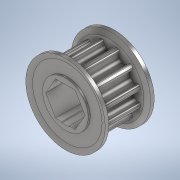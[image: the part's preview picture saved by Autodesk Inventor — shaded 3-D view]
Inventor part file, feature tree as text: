
AUTODESK INVENTOR PART (.ipt)
format: ipt  version: 2020 (Build 240168000, 168)  size: 256,512 bytes
history: native  units: in
note: dims shown in document units (in); Inventor stores cm internally (conversion verified against a paired STEP export)
features: extrude x2, sketch x2, other x1
ambient origin geometry x8: Origin, YZ Plane, XZ Plane, XY Plane, X Axis, Y Axis, Z Axis, Center Point
bodies: Solid1 (feature_tree)
feature tree (5):
  extrude  "Extrusion3"  TaperAngle=0.0deg  [1 undecoded]
  extrude  "Extrusion4"  [1 undecoded]
  sketch  "Sketch3"  dims[d5=0.375in d6=0.0in d7=0.0in]
  sketch  "Sketch4"  dims[d8=1.0in d9=0.0in]
  other  "Cut-Extrude2"
note: 2 required parameter values undecoded (feature->parameter linkage not recoverable at this tier; creation-order binding heuristic only, values carry confidence <= 0.55)
